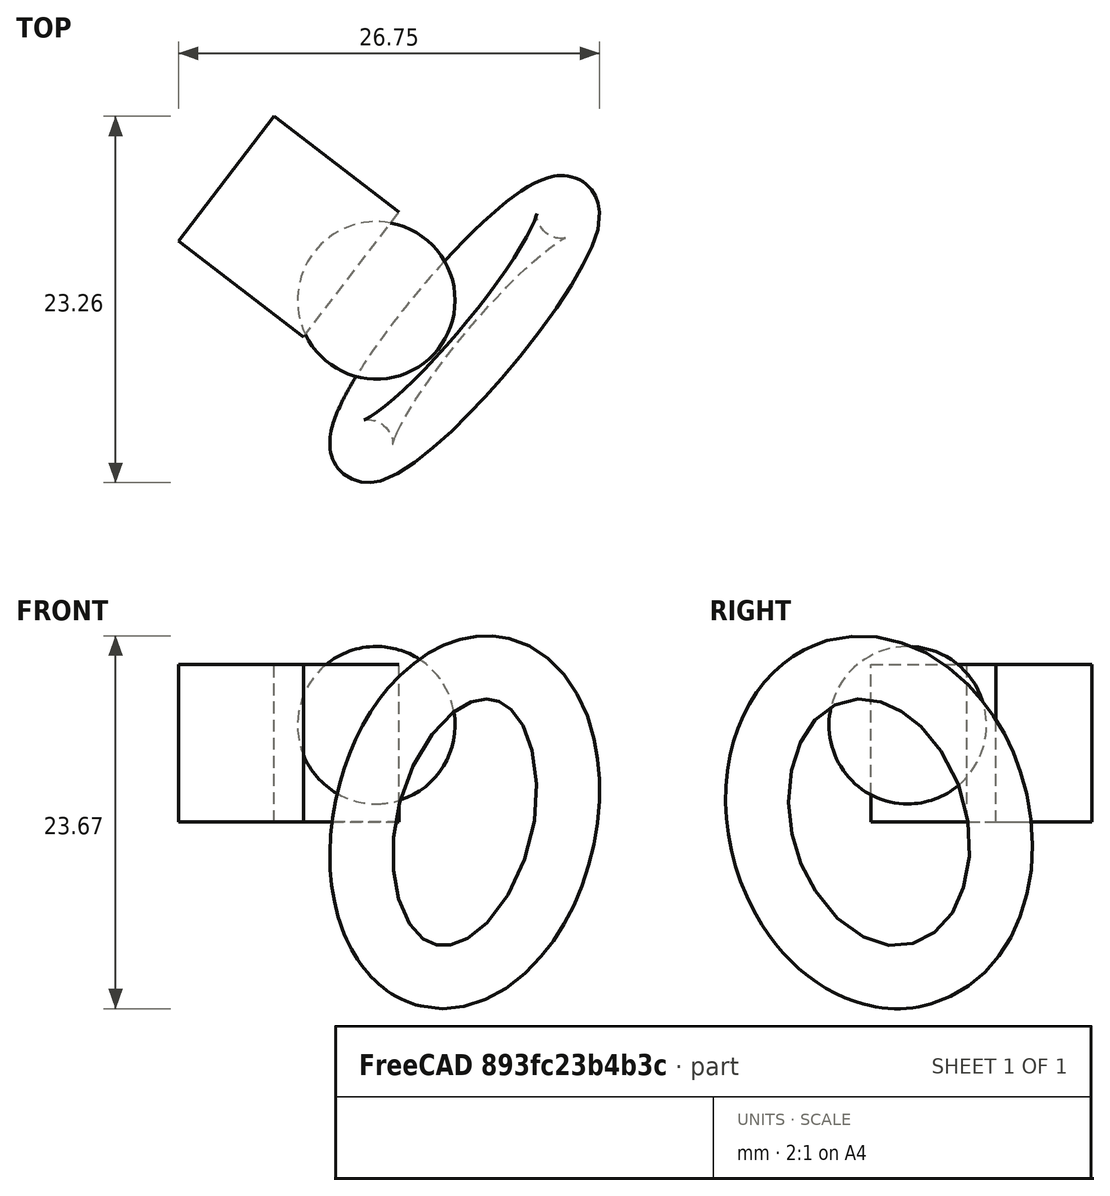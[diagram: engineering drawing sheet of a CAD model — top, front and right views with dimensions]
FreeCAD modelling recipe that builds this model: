
FCSTD DOCUMENT  (FreeCAD 0.18R16146 (Git))
Label: test_freecad_0.18_macos
License: All rights reserved
LicenseURL: http://en.wikipedia.org/wiki/All_rights_reserved
objects: Part::Box×1, Part::Sphere×1, Part::Torus×1
note: 3 computed .brp shape members not serialized (recipe doc carries the construction recipe); baked Part::Feature solids carry a one-line shape summary decoded from their .brp

FEATURE [Part::Box] Box  label="Cube"
  AttacherType = Attacher::AttachEngine3D
  Height = 10
  Length = 10
  Placement = pos=(-8.43103,5.6118,0) rot=(0,0,1;0.917309rad)
  Width = 10
FEATURE [Part::Sphere] Sphere
  Angle1 = -90
  Angle2 = 90
  Angle3 = 360
  AttacherType = Attacher::AttachEngine3D
  Placement = pos=(-3.80212,7.93985,6.15636) rot=(0,0,1;0rad)
  Radius = 5
FEATURE [Part::Torus] Torus
  Angle1 = -180
  Angle2 = 180
  Angle3 = 360
  AttacherType = Attacher::AttachEngine3D
  Placement = pos=(1.81483,6.1184,-0.0135018) rot=(-0.429336,0.479938,0.765069;3.36189rad)
  Radius1 = 10
  Radius2 = 2
